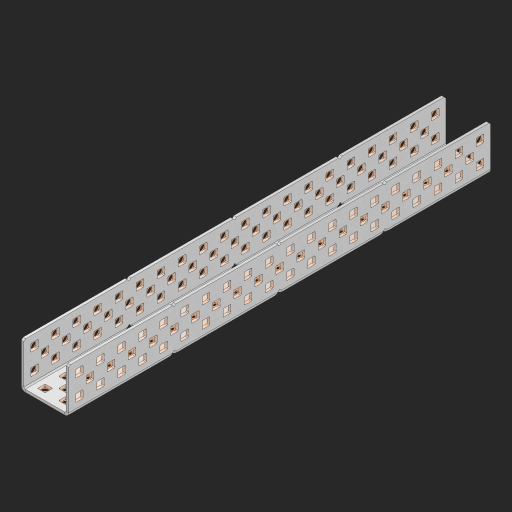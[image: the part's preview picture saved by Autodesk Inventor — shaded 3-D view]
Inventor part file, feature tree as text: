
AUTODESK INVENTOR PART (.ipt)
format: ipt  version: 2023 (Build 270158000, 158)  size: 2,222,592 bytes
history: native  units: in
note: dims shown in document units (in); Inventor stores cm internally (conversion verified against a paired STEP export)
features: other x242, extrude x234, sheet_metal_op x8, sketch x7, mirror x3, pattern_linear x2, chamfer x1
ambient origin geometry x8: Origin, YZ Plane, XZ Plane, XY Plane, X Axis, Y Axis, Z Axis, Center Point
bodies: Solid1 (feature_tree), Body (feature_tree)
feature tree (497):
  sheet_metal_op  "Flanges"
  sheet_metal_op  "Body Pattern"
  pattern_linear  "Center Pattern"  Spacing1=1.0in  [1 undecoded]
  other  "Arc Length"
  mirror  "Notch Mirror"
  pattern_linear  "Notch Pattern"  Spacing1=0.25in  [1 undecoded]
  other  "Diagonal Plane"
  mirror  "Flange 1"
  mirror  "Flange 2"
  chamfer  "End Chamfer"
  sketch  "Sketch1"  dims[d0=1.0in]
  other  "Plate1"
  sketch  "Sketch2"  dims[d1=10.0in]
  other  "Plate2"
  sheet_metal_op  "Bend1"
  sheet_metal_op  "Corner1"
  sketch  "Sketch8"  dims[d2=0.0625in]
  sketch  "Sketch9"  dims[d3=0.0625in]
  other  "Srf91"
  sheet_metal_op  "Body Pattern Sketch"
  other  "Srf92"
  sketch  "Sketch13"  dims[d4=0.0312in]
  sketch  "Sketch15"  dims[d5=0.125in]
  sketch  "Sketch16"  dims[d6=0.0625in d7=1.0in d8=90.0deg d9=0.0312in d10=0.25in d11=0.0625in d12=0.0625in d49=0.182in d50=0.02in d52=0.25in d53=0.0625in d54=0.0in d55=0.172in d56=1.0in d57=0.0in d60=7.874in d62=0.5in d63=0.7874in d65=0.5in d85=0.1473in d86=0.1782in d88=0.04in d89=0.0625in d90=0.0in d91=0.04in d92=0.0491in d95=2.5in d96=0.04in d97=0.25in d98=45.0deg d99=0.25in d102=2.497in d106=0.182in d107=0.02in d108=0.5in d110=0.0625in d111=0.0in d112=0.172in d113=0.5in d114=0.0in d117=0.5in d118=0.5in d131=0.25in d132=0.25in]
  other  "Srf786"
  other  "Srf889"
  other  "Srf890"
  other  "Srf891"
  other  "Srf892"
  other  "Srf893"
  other  "Srf894"
  other  "Srf895"
  other  "Srf896"
  other  "Srf996"
  other  "Srf997"
  other  "Srf998"
  other  "Srf999"
  other  "Srf1000"
  other  "Srf1255"
  other  "Srf1256"
  other  "Srf1257"
  other  "Srf1258"
  other  "Srf1259"
  other  "Srf1315"
  other  "Srf1316"
  other  "Srf1317"
  other  "Srf1325"
  other  "Srf1326"
  other  "Srf1327"
  other  "Srf1328"
  other  "Srf1329"
  other  "Srf1330"
  other  "Srf1331"
  other  "Srf1332"
  other  "Srf1338"
  other  "Srf1339"
  other  "Srf1340"
  other  "Srf1341"
  other  "Srf1342"
  other  "Srf1369"
  other  "Srf1370"
  other  "Srf1371"
  other  "Srf1372"
  other  "Srf1373"
  other  "Srf1374"
  other  "Srf1375"
  other  "Srf1376"
  other  "Srf1384"
  other  "Srf1385"
  other  "Srf1386"
  other  "Srf1387"
  other  "Srf1388"
  other  "Srf1389"
  other  "Srf1390"
  other  "Srf1391"
  other  "Srf1397"
  other  "Srf1398"
  other  "Srf1399"
  other  "Srf1400"
  other  "Srf1401"
  other  "Srf1428"
  other  "Srf1429"
  other  "Srf1430"
  other  "Srf1431"
  other  "Srf1432"
  other  "Srf1433"
  other  "Srf1434"
  other  "Srf1473"
  other  "Srf1474"
  other  "Srf1475"
  other  "Srf1476"
  other  "Srf1477"
  other  "Srf1478"
  other  "Srf1479"
  other  "Srf1480"
  other  "Srf1481"
  other  "Srf1482"
  other  "Srf1483"
  other  "Srf1484"
  other  "Srf1485"
  other  "Srf1486"
  other  "Srf1487"
  other  "Srf1488"
  other  "Srf1489"
  other  "Srf1490"
  other  "Srf1491"
  other  "Srf1500"
  other  "Srf1501"
  other  "Srf1502"
  other  "Srf1503"
  other  "Srf1504"
  other  "Srf1505"
  other  "Srf1506"
  other  "Srf1507"
  other  "Srf1508"
  other  "Srf1509"
  other  "Srf1510"
  other  "Srf1511"
  other  "Srf1512"
  other  "Srf1513"
  other  "Srf1514"
  other  "Srf1515"
  other  "Srf1516"
  other  "Srf1517"
  other  "Srf1518"
  other  "Srf1519"
  other  "Srf1520"
  other  "Srf1521"
  other  "Srf1522"
  other  "Srf1523"
  other  "Srf1524"
  other  "Srf1525"
  other  "Srf1526"
  other  "Srf1527"
  other  "Srf1528"
  other  "Srf1529"
  other  "Srf1530"
  other  "Srf1531"
  other  "Srf1532"
  other  "Srf1533"
  other  "Srf1534"
  other  "Srf1535"
  other  "Srf1536"
  other  "Srf1537"
  other  "Srf1538"
  other  "Srf1539"
  other  "Srf1540"
  other  "Srf1541"
  other  "Srf1542"
  other  "Srf1543"
  other  "Srf1544"
  other  "Srf1545"
  other  "Srf1546"
  other  "Srf1547"
  other  "Srf1548"
  other  "Srf1549"
  other  "Srf1550"
  other  "Srf1551"
  other  "Srf1552"
  other  "Srf1553"
  other  "Srf1554"
  other  "Srf1555"
  other  "Srf1556"
  other  "Srf1557"
  other  "Srf1558"
  other  "Srf1559"
  other  "Srf1560"
  other  "Srf1561"
  other  "Srf1562"
  other  "Srf1563"
  other  "Srf1564"
  other  "Srf1565"
  other  "Srf1566"
  other  "Srf1567"
  other  "Srf1568"
  other  "Srf1569"
  other  "Srf1570"
  other  "Srf1571"
  other  "Srf1572"
  other  "Srf1573"
  other  "Srf1574"
  other  "Srf1575"
  other  "Srf1576"
  other  "Srf1577"
  other  "Srf1578"
  other  "Srf1579"
  other  "Srf1580"
  other  "Srf1581"
  other  "Srf1582"
  other  "Srf1583"
  other  "Srf1584"
  other  "Srf1585"
  other  "Srf1586"
  other  "Srf1587"
  other  "Srf1588"
  other  "Srf1589"
  other  "Srf1590"
  other  "Srf1591"
  other  "Srf1592"
  other  "Srf1593"
  other  "Srf1594"
  other  "Srf1595"
  other  "Srf1596"
  other  "Srf1597"
  other  "Srf1598"
  other  "Srf1599"
  other  "Srf1600"
  other  "Srf1601"
  other  "Srf1602"
  other  "Srf1603"
  other  "Srf1604"
  other  "Srf1605"
  other  "Srf1606"
  other  "Srf1607"
  other  "Srf1608"
  other  "Srf1609"
  other  "Srf1610"
  other  "Srf1611"
  other  "Srf1612"
  other  "Srf1613"
  other  "Srf1614"
  other  "Srf1615"
  other  "Srf1616"
  other  "Srf1617"
  other  "Srf1618"
  other  "Srf1619"
  other  "Srf1620"
  other  "Srf1621"
  other  "Srf1622"
  other  "Srf1623"
  other  "Srf1624"
  other  "Srf1625"
  other  "Srf1626"
  other  "Srf1627"
  other  "Srf1628"
  other  "Srf1629"
  other  "Srf1630"
  other  "Srf1631"
  other  "Srf1632"
  other  "Srf1633"
  other  "Srf1634"
  other  "Srf1635"
  other  "Srf1636"
  other  "Srf1637"
  other  "Srf1638"
  other  "Srf1639"
  other  "Srf1640"
  other  "Srf1641"
  other  "Srf1642"
  other  "Srf1643"
  other  "Srf1644"
  other  "Srf1645"
  other  "Srf1646"
  other  "Srf1647"
  other  "Srf1648"
  other  "Srf1649"
  other  "Srf1650"
  other  "Srf1651"
  sheet_metal_op  "Body Stamp"
  sheet_metal_op  "Body Circle"
  other  "Center Stamp"
  other  "Center Circle"
  sheet_metal_op  "Notch"
  extrude  "ExtrusionSrf92"  Depth=0.0625in
  extrude  "ExtrusionSrf889"  Depth=0.0625in
  extrude  "ExtrusionSrf890"  Depth=0.5in
  extrude  "ExtrusionSrf891"  Depth=0.02in
  extrude  "ExtrusionSrf892"  Depth=0.5in
  extrude  "ExtrusionSrf893"  Depth=0.0625in
  extrude  "ExtrusionSrf894"  TaperAngle=0.0deg  [1 undecoded]
  extrude  "ExtrusionSrf895"  Depth=0.5in
  extrude  "ExtrusionSrf896"  Depth=1.0in TaperAngle=0.0deg
  extrude  "ExtrusionSrf996"  Depth=0.5in
  extrude  "ExtrusionSrf997"  Depth=0.5in
  extrude  "ExtrusionSrf998"  Depth=0.5in
  extrude  "ExtrusionSrf999"  Depth=0.5in
  extrude  "ExtrusionSrf1000"  Depth=0.5in
  extrude  "ExtrusionSrf1255"  Depth=0.0625in
  extrude  "ExtrusionSrf1256"  TaperAngle=0.0deg  [1 undecoded]
  extrude  "ExtrusionSrf1257"  Depth=0.5in
  extrude  "ExtrusionSrf1258"  Depth=0.5in
  extrude  "ExtrusionSrf1259"  Depth=2.5in
  extrude  "ExtrusionSrf1315"  Depth=0.5in TaperAngle=45.0deg
  extrude  "ExtrusionSrf1316"  Depth=0.5in
  extrude  "ExtrusionSrf1355"  Depth=0.5in
  extrude  "ExtrusionSrf1356"  Depth=0.5in
  extrude  "ExtrusionSrf1357"  Depth=0.02in
  extrude  "ExtrusionSrf1358"  Depth=0.5in
  extrude  "ExtrusionSrf1359"  Depth=0.0625in
  extrude  "ExtrusionSrf1360"  TaperAngle=0.0deg  [1 undecoded]
  extrude  "ExtrusionSrf1361"  Depth=0.5in
  extrude  "ExtrusionSrf1362"  Depth=0.5in TaperAngle=0.0deg
  extrude  "ExtrusionSrf1363"  Depth=0.5in
  extrude  "ExtrusionSrf1364"  Depth=0.5in
  extrude  "ExtrusionSrf1365"  Depth=0.5in
  extrude  "ExtrusionSrf1366"  Depth=0.5in
  extrude  "ExtrusionSrf1367"  [1 undecoded]
  extrude  "ExtrusionSrf1368"  [1 undecoded]
  extrude  "ExtrusionSrf1369"  [1 undecoded]
  extrude  "ExtrusionSrf1370"  [1 undecoded]
  extrude  "ExtrusionSrf1371"  [1 undecoded]
  extrude  "ExtrusionSrf1372"  [1 undecoded]
  extrude  "ExtrusionSrf1373"  [1 undecoded]
  extrude  "ExtrusionSrf1374"  [1 undecoded]
  extrude  "ExtrusionSrf1375"  [1 undecoded]
  extrude  "ExtrusionSrf1414"  [1 undecoded]
  extrude  "ExtrusionSrf1415"  [1 undecoded]
  extrude  "ExtrusionSrf1416"  [1 undecoded]
  extrude  "ExtrusionSrf1417"  [1 undecoded]
  extrude  "ExtrusionSrf1418"  [1 undecoded]
  extrude  "ExtrusionSrf1419"  [1 undecoded]
  extrude  "ExtrusionSrf1420"  [1 undecoded]
  extrude  "ExtrusionSrf1421"  [1 undecoded]
  extrude  "ExtrusionSrf1422"  [1 undecoded]
  extrude  "ExtrusionSrf1423"  [1 undecoded]
  extrude  "ExtrusionSrf1424"  [1 undecoded]
  extrude  "ExtrusionSrf1425"  [1 undecoded]
  extrude  "ExtrusionSrf1426"  [1 undecoded]
  extrude  "ExtrusionSrf1427"  [1 undecoded]
  extrude  "ExtrusionSrf1428"  [1 undecoded]
  extrude  "ExtrusionSrf1429"  [1 undecoded]
  extrude  "ExtrusionSrf1430"  [1 undecoded]
  extrude  "ExtrusionSrf1431"  [1 undecoded]
  extrude  "ExtrusionSrf1432"  [1 undecoded]
  extrude  "ExtrusionSrf1433"  [1 undecoded]
  extrude  "ExtrusionSrf1434"  [1 undecoded]
  extrude  "ExtrusionSrf1473"  [1 undecoded]
  extrude  "ExtrusionSrf1474"  [1 undecoded]
  extrude  "ExtrusionSrf1475"  [1 undecoded]
  extrude  "ExtrusionSrf1476"  [1 undecoded]
  extrude  "ExtrusionSrf1477"  [1 undecoded]
  extrude  "ExtrusionSrf1478"  [1 undecoded]
  extrude  "ExtrusionSrf1479"  [1 undecoded]
  extrude  "ExtrusionSrf1480"  [1 undecoded]
  extrude  "ExtrusionSrf1481"  [1 undecoded]
  extrude  "ExtrusionSrf1482"  [1 undecoded]
  extrude  "ExtrusionSrf1483"  [1 undecoded]
  extrude  "ExtrusionSrf1484"  [1 undecoded]
  extrude  "ExtrusionSrf1485"  [1 undecoded]
  extrude  "ExtrusionSrf1486"  [1 undecoded]
  extrude  "ExtrusionSrf1487"  [1 undecoded]
  extrude  "ExtrusionSrf1488"  [1 undecoded]
  extrude  "ExtrusionSrf1489"  [1 undecoded]
  extrude  "ExtrusionSrf1490"  [1 undecoded]
  extrude  "ExtrusionSrf1491"  [1 undecoded]
  extrude  "ExtrusionSrf1500"  [1 undecoded]
  extrude  "ExtrusionSrf1501"  [1 undecoded]
  extrude  "ExtrusionSrf1502"  [1 undecoded]
  extrude  "ExtrusionSrf1503"  [1 undecoded]
  extrude  "ExtrusionSrf1504"  [1 undecoded]
  extrude  "ExtrusionSrf1505"  [1 undecoded]
  extrude  "ExtrusionSrf1506"  [1 undecoded]
  extrude  "ExtrusionSrf1507"  [1 undecoded]
  extrude  "ExtrusionSrf1508"  [1 undecoded]
  extrude  "ExtrusionSrf1509"  [1 undecoded]
  extrude  "ExtrusionSrf1510"  [1 undecoded]
  extrude  "ExtrusionSrf1511"  [1 undecoded]
  extrude  "ExtrusionSrf1512"  [1 undecoded]
  extrude  "ExtrusionSrf1513"  [1 undecoded]
  extrude  "ExtrusionSrf1514"  [1 undecoded]
  extrude  "ExtrusionSrf1515"  [1 undecoded]
  extrude  "ExtrusionSrf1516"  [1 undecoded]
  extrude  "ExtrusionSrf1517"  [1 undecoded]
  extrude  "ExtrusionSrf1518"  [1 undecoded]
  extrude  "ExtrusionSrf1519"  [1 undecoded]
  extrude  "ExtrusionSrf1520"  [1 undecoded]
  extrude  "ExtrusionSrf1521"  [1 undecoded]
  extrude  "ExtrusionSrf1522"  [1 undecoded]
  extrude  "ExtrusionSrf1523"  [1 undecoded]
  extrude  "ExtrusionSrf1524"  [1 undecoded]
  extrude  "ExtrusionSrf1525"  [1 undecoded]
  extrude  "ExtrusionSrf1526"  [1 undecoded]
  extrude  "ExtrusionSrf1527"  [1 undecoded]
  extrude  "ExtrusionSrf1528"  [1 undecoded]
  extrude  "ExtrusionSrf1529"  [1 undecoded]
  extrude  "ExtrusionSrf1530"  [1 undecoded]
  extrude  "ExtrusionSrf1531"  [1 undecoded]
  extrude  "ExtrusionSrf1532"  [1 undecoded]
  extrude  "ExtrusionSrf1533"  [1 undecoded]
  extrude  "ExtrusionSrf1534"  [1 undecoded]
  extrude  "ExtrusionSrf1535"  [1 undecoded]
  extrude  "ExtrusionSrf1536"  [1 undecoded]
  extrude  "ExtrusionSrf1537"  [1 undecoded]
  extrude  "ExtrusionSrf1538"  [1 undecoded]
  extrude  "ExtrusionSrf1539"  [1 undecoded]
  extrude  "ExtrusionSrf1540"  [1 undecoded]
  extrude  "ExtrusionSrf1541"  [1 undecoded]
  extrude  "ExtrusionSrf1542"  [1 undecoded]
  extrude  "ExtrusionSrf1543"  [1 undecoded]
  extrude  "ExtrusionSrf1544"  [1 undecoded]
  extrude  "ExtrusionSrf1545"  [1 undecoded]
  extrude  "ExtrusionSrf1546"  [1 undecoded]
  extrude  "ExtrusionSrf1547"  [1 undecoded]
  extrude  "ExtrusionSrf1548"  [1 undecoded]
  extrude  "ExtrusionSrf1549"  [1 undecoded]
  extrude  "ExtrusionSrf1550"  [1 undecoded]
  extrude  "ExtrusionSrf1551"  [1 undecoded]
  extrude  "ExtrusionSrf1552"  [1 undecoded]
  extrude  "ExtrusionSrf1553"  [1 undecoded]
  extrude  "ExtrusionSrf1554"  [1 undecoded]
  extrude  "ExtrusionSrf1555"  [1 undecoded]
  extrude  "ExtrusionSrf1556"  [1 undecoded]
  extrude  "ExtrusionSrf1557"  [1 undecoded]
  extrude  "ExtrusionSrf1558"  [1 undecoded]
  extrude  "ExtrusionSrf1559"  [1 undecoded]
  extrude  "ExtrusionSrf1560"  [1 undecoded]
  extrude  "ExtrusionSrf1561"  [1 undecoded]
  extrude  "ExtrusionSrf1562"  [1 undecoded]
  extrude  "ExtrusionSrf1563"  [1 undecoded]
  extrude  "ExtrusionSrf1564"  [1 undecoded]
  extrude  "ExtrusionSrf1565"  [1 undecoded]
  extrude  "ExtrusionSrf1566"  [1 undecoded]
  extrude  "ExtrusionSrf1567"  [1 undecoded]
  extrude  "ExtrusionSrf1568"  [1 undecoded]
  extrude  "ExtrusionSrf1569"  [1 undecoded]
  extrude  "ExtrusionSrf1570"  [1 undecoded]
  extrude  "ExtrusionSrf1571"  [1 undecoded]
  extrude  "ExtrusionSrf1572"  [1 undecoded]
  extrude  "ExtrusionSrf1573"  [1 undecoded]
  extrude  "ExtrusionSrf1574"  [1 undecoded]
  extrude  "ExtrusionSrf1575"  [1 undecoded]
  extrude  "ExtrusionSrf1576"  [1 undecoded]
  extrude  "ExtrusionSrf1577"  [1 undecoded]
  extrude  "ExtrusionSrf1578"  [1 undecoded]
  extrude  "ExtrusionSrf1579"  [1 undecoded]
  extrude  "ExtrusionSrf1580"  [1 undecoded]
  extrude  "ExtrusionSrf1581"  [1 undecoded]
  extrude  "ExtrusionSrf1582"  [1 undecoded]
  extrude  "ExtrusionSrf1583"  [1 undecoded]
  extrude  "ExtrusionSrf1584"  [1 undecoded]
  extrude  "ExtrusionSrf1585"  [1 undecoded]
  extrude  "ExtrusionSrf1586"  [1 undecoded]
  extrude  "ExtrusionSrf1587"  [1 undecoded]
  extrude  "ExtrusionSrf1588"  [1 undecoded]
  extrude  "ExtrusionSrf1589"  [1 undecoded]
  extrude  "ExtrusionSrf1590"  [1 undecoded]
  extrude  "ExtrusionSrf1591"  [1 undecoded]
  extrude  "ExtrusionSrf1592"  [1 undecoded]
  extrude  "ExtrusionSrf1593"  [1 undecoded]
  extrude  "ExtrusionSrf1594"  [1 undecoded]
  extrude  "ExtrusionSrf1595"  [1 undecoded]
  extrude  "ExtrusionSrf1596"  [1 undecoded]
  extrude  "ExtrusionSrf1597"  [1 undecoded]
  extrude  "ExtrusionSrf1598"  [1 undecoded]
  extrude  "ExtrusionSrf1599"  [1 undecoded]
  extrude  "ExtrusionSrf1600"  [1 undecoded]
  extrude  "ExtrusionSrf1601"  [1 undecoded]
  extrude  "ExtrusionSrf1602"  [1 undecoded]
  extrude  "ExtrusionSrf1603"  [1 undecoded]
  extrude  "ExtrusionSrf1604"  [1 undecoded]
  extrude  "ExtrusionSrf1605"  [1 undecoded]
  extrude  "ExtrusionSrf1606"  [1 undecoded]
  extrude  "ExtrusionSrf1607"  [1 undecoded]
  extrude  "ExtrusionSrf1608"  [1 undecoded]
  extrude  "ExtrusionSrf1609"  [1 undecoded]
  extrude  "ExtrusionSrf1610"  [1 undecoded]
  extrude  "ExtrusionSrf1611"  [1 undecoded]
  extrude  "ExtrusionSrf1612"  [1 undecoded]
  extrude  "ExtrusionSrf1613"  [1 undecoded]
  extrude  "ExtrusionSrf1614"  [1 undecoded]
  extrude  "ExtrusionSrf1615"  [1 undecoded]
  extrude  "ExtrusionSrf1616"  [1 undecoded]
  extrude  "ExtrusionSrf1617"  [1 undecoded]
  extrude  "ExtrusionSrf1618"  [1 undecoded]
  extrude  "ExtrusionSrf1619"  [1 undecoded]
  extrude  "ExtrusionSrf1620"  [1 undecoded]
  extrude  "ExtrusionSrf1621"  [1 undecoded]
  extrude  "ExtrusionSrf1622"  [1 undecoded]
  extrude  "ExtrusionSrf1623"  [1 undecoded]
  extrude  "ExtrusionSrf1624"  [1 undecoded]
  extrude  "ExtrusionSrf1625"  [1 undecoded]
  extrude  "ExtrusionSrf1626"  [1 undecoded]
  extrude  "ExtrusionSrf1627"  [1 undecoded]
  extrude  "ExtrusionSrf1628"  [1 undecoded]
  extrude  "ExtrusionSrf1629"  [1 undecoded]
  extrude  "ExtrusionSrf1630"  [1 undecoded]
  extrude  "ExtrusionSrf1631"  [1 undecoded]
  extrude  "ExtrusionSrf1632"  [1 undecoded]
  extrude  "ExtrusionSrf1633"  [1 undecoded]
  extrude  "ExtrusionSrf1634"  [1 undecoded]
  extrude  "ExtrusionSrf1635"  [1 undecoded]
  extrude  "ExtrusionSrf1636"  [1 undecoded]
  extrude  "ExtrusionSrf1637"  [1 undecoded]
  extrude  "ExtrusionSrf1638"  [1 undecoded]
  extrude  "ExtrusionSrf1639"  [1 undecoded]
  extrude  "ExtrusionSrf1640"  [1 undecoded]
  extrude  "ExtrusionSrf1641"  [1 undecoded]
  extrude  "ExtrusionSrf1642"  [1 undecoded]
  extrude  "ExtrusionSrf1643"  [1 undecoded]
  extrude  "ExtrusionSrf1644"  [1 undecoded]
  extrude  "ExtrusionSrf1645"  [1 undecoded]
  extrude  "ExtrusionSrf1646"  [1 undecoded]
  extrude  "ExtrusionSrf1647"  [1 undecoded]
  extrude  "ExtrusionSrf1648"  [1 undecoded]
  extrude  "ExtrusionSrf1649"  [1 undecoded]
  extrude  "ExtrusionSrf1650"  [1 undecoded]
  extrude  "ExtrusionSrf1651"  [1 undecoded]
note: 206 required parameter values undecoded (feature->parameter linkage not recoverable at this tier; creation-order binding heuristic only, values carry confidence <= 0.55)
